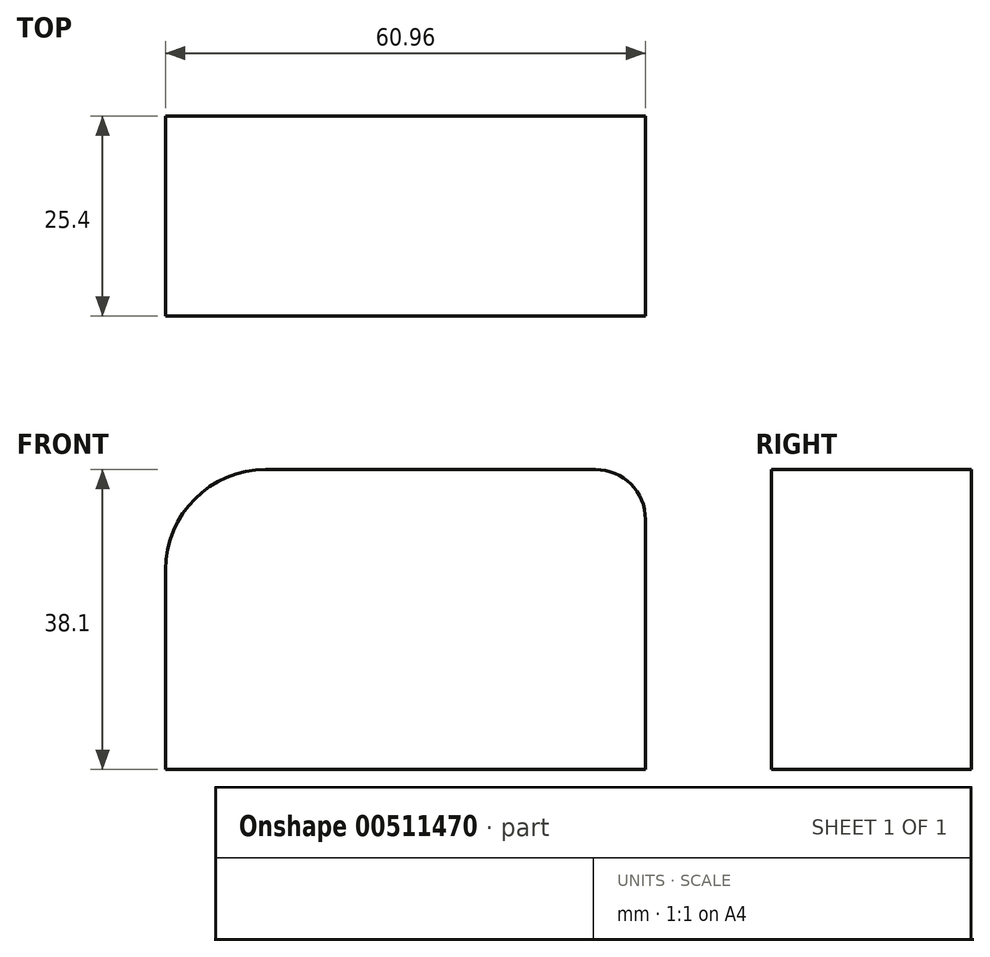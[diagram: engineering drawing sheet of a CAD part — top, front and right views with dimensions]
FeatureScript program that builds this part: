
annotation { "Feature Type Name" : "Feature", "Feature Type Description" : "" }
export const myFeature = defineFeature(function(context is Context, id is Id, definition is map)
    precondition{}
    {
        {
            var Q0;
            Q0=qCreatedBy(makeId("Front.planeOp"),FACE);
            var sketch = newSketch(context, id + "F0", { "sketchPlane" : qUnion([Q0])});
            skLineSegment(sketch, "E0.bottom", {"start": v(-37.03, 70.18) * mm, "end": v(4.88, 70.18) * mm});
            skLineSegment(sketch, "E0.top", {"start": v(-49.73, 32.08) * mm, "end": v(11.23, 32.08) * mm});
            skLineSegment(sketch, "E0.left", {"start": v(-49.73, 57.48) * mm, "end": v(-49.73, 32.08) * mm});
            skLineSegment(sketch, "E0.right", {"start": v(11.23, 63.83) * mm, "end": v(11.23, 32.08) * mm});
            skLineSegment(sketch, "E1", {"start": v(11.23, 32.08) * mm, "end": v(52.04, 13.27) * mm});
            skPoint(sketch, "E2.visualSharp", {"position": v(11.23, 70.18) * mm});
            skArc(sketch, "E2.filletArc", {"start": v(11.23, 63.83) * mm, "mid": v(9.37, 68.32) * mm, "end": v(4.88, 70.18) * mm});
            skPoint(sketch, "E3.visualSharp", {"position": v(-49.73, 70.18) * mm});
            skArc(sketch, "E3.filletArc", {"start": v(-37.03, 70.18) * mm, "mid": v(-46.01, 66.46) * mm, "end": v(-49.73, 57.48) * mm});
            skLineSegment(sketch, "E4.0", {"start": v(-49.73, 25.73) * mm, "end": v(11.23, 25.73) * mm});
            skArc(sketch, "E5", {"start": v(52.04, 13.27) * mm, "mid": v(92.07, 37.16) * mm, "end": v(55.35, 65.88) * mm});
            skArc(sketch, "E6", {"start": v(127.53, -3.91) * mm, "mid": v(147.04, 50.47) * mm, "end": v(91.68, 33.94) * mm});
            skSolve(sketch);
        }
        {
            var Q0;
            Q0 = qSketchRegion(id + "F0", true);
            extrude(context, id + "F1", {"entities" : qUnion([Q0]), "depth" : 25.4 * mm});
        }
    });
